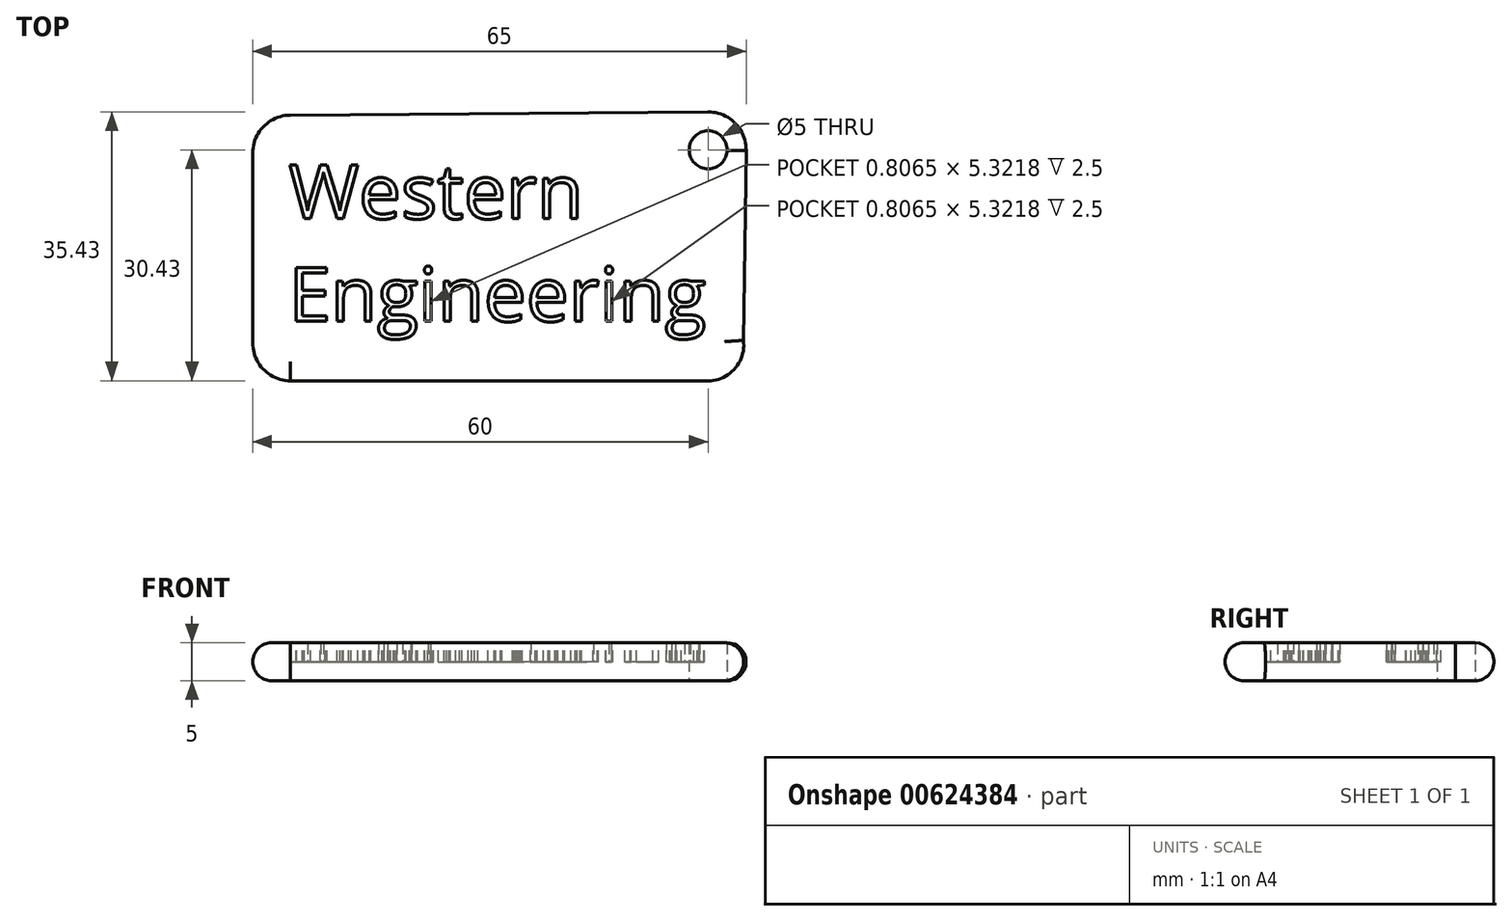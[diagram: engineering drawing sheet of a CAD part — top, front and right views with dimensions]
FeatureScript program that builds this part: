
annotation { "Feature Type Name" : "Feature", "Feature Type Description" : "" }
export const myFeature = defineFeature(function(context is Context, id is Id, definition is map)
    precondition{}
    {
        {
            var Q0;
            Q0=qCreatedBy(makeId("Top.planeOp"),FACE);
            var sketch = newSketch(context, id + "F0", { "sketchPlane" : qUnion([Q0])});
            skLineSegment(sketch, "E0", {"start": v(0, 5) * mm, "end": v(0, 30) * mm});
            skArc(sketch, "E1", {"start": v(0, 30) * mm, "mid": v(1.45, 33.52) * mm, "end": v(4.96, 35) * mm});
            skArc(sketch, "E2", {"start": v(0, 5) * mm, "mid": v(1.45, 1.48) * mm, "end": v(4.96, 0) * mm});
            skLineSegment(sketch, "E3", {"start": v(4.96, 35) * mm, "end": v(59.96, 35.43) * mm});
            skLineSegment(sketch, "E4", {"start": v(4.96, 0) * mm, "end": v(59.96, 0) * mm});
            skArc(sketch, "E5", {"start": v(59.96, 35.43) * mm, "mid": v(63.56, 33.94) * mm, "end": v(65, 30.33) * mm});
            skArc(sketch, "E6", {"start": v(59.96, 0) * mm, "mid": v(63.5, 1.6) * mm, "end": v(64.64, 5.33) * mm});
            skLineSegment(sketch, "E7", {"start": v(65, 30.33) * mm, "end": v(64.64, 5.33) * mm});
            skCircle(sketch, "E8", {"center": v(60, 30.43) * mm, "radius": 2.5 * mm});
            skSolve(sketch);
        }
        {
            var Q0;
            Q0=makeQuery(id+"F0.imprint","IMPRINT",FACE,{"disambiguationData":[TD([[makeQuery(id+"F0.imprint","IMPRINT",EDGE,{"derivedFrom":sQuery(id+"F0.wireOp",EDGE,"E0")}),-1.0]])]});
            extrude(context, id + "F1", {"entities" : qUnion([Q0]), "depth" : 5 * mm, "offsetDistance" : 25 * mm});
        }
        {
            var Q0;
            Q0=makeQuery(id+"F1.opExtrude","CAP_EDGE",EDGE,{"disambiguationData":[OSD([sQuery(id+"F0.wireOp",EDGE,"E3")])],"isStart":false});
            var Q1;
            Q1=makeQuery(id+"F1.opExtrude","CAP_EDGE",EDGE,{"disambiguationData":[OSD([sQuery(id+"F0.wireOp",EDGE,"E5")])],"isStart":false});
            var Q2;
            Q2=makeQuery(id+"F1.opExtrude","CAP_EDGE",EDGE,{"disambiguationData":[OSD([sQuery(id+"F0.wireOp",EDGE,"E7")])],"isStart":false});
            var Q3;
            Q3=makeQuery(id+"F1.opExtrude","CAP_EDGE",EDGE,{"disambiguationData":[OSD([sQuery(id+"F0.wireOp",EDGE,"E2")])],"isStart":false});
            var Q4;
            Q4=makeQuery(id+"F1.opExtrude","CAP_EDGE",EDGE,{"disambiguationData":[OSD([sQuery(id+"F0.wireOp",EDGE,"E1")])],"isStart":false});
            var Q5;
            Q5=makeQuery(id+"F1.opExtrude","CAP_EDGE",EDGE,{"disambiguationData":[OSD([sQuery(id+"F0.wireOp",EDGE,"E6")])],"isStart":false});
            fillet(context, id + "F2", {"entities" : qUnion([Q0, Q1, Q2, Q3, Q4, Q5]), "radius" : 2.5 * mm, "tangentPropagation" : true, "allowEdgeOverflow" : false});
        }
        {
            var Q0;
            Q0=makeQuery(id+"F1.opExtrude","CAP_EDGE",EDGE,{"disambiguationData":[OSD([sQuery(id+"F0.wireOp",EDGE,"E6")])],"isStart":true});
            var Q1;
            Q1=makeQuery(id+"F1.opExtrude","CAP_EDGE",EDGE,{"disambiguationData":[OSD([sQuery(id+"F0.wireOp",EDGE,"E7")])],"isStart":true});
            var Q2;
            Q2=makeQuery(id+"F1.opExtrude","CAP_EDGE",EDGE,{"disambiguationData":[OSD([sQuery(id+"F0.wireOp",EDGE,"E3")])],"isStart":true});
            var Q3;
            Q3=makeQuery(id+"F1.opExtrude","CAP_EDGE",EDGE,{"disambiguationData":[OSD([sQuery(id+"F0.wireOp",EDGE,"E5")])],"isStart":true});
            var Q4;
            Q4=makeQuery(id+"F1.opExtrude","CAP_EDGE",EDGE,{"disambiguationData":[OSD([sQuery(id+"F0.wireOp",EDGE,"E1")])],"isStart":true});
            var Q5;
            Q5=makeQuery(id+"F1.opExtrude","CAP_EDGE",EDGE,{"disambiguationData":[OSD([sQuery(id+"F0.wireOp",EDGE,"E0")])],"isStart":true});
            var Q6;
            Q6=makeQuery(id+"F1.opExtrude","CAP_EDGE",EDGE,{"disambiguationData":[OSD([sQuery(id+"F0.wireOp",EDGE,"E2")])],"isStart":true});
            fillet(context, id + "F3", {"entities" : qUnion([Q0, Q1, Q2, Q3, Q4, Q5, Q6]), "radius" : 2.5 * mm, "tangentPropagation" : true, "allowEdgeOverflow" : false});
        }
        {
            var Q0;
            Q0=makeQuery(id+"F1.opExtrude","CAP_FACE",FACE,{"disambiguationData":[OSD([sQuery(id+"F0.wireOp",EDGE,"E0"),sQuery(id+"F0.wireOp",EDGE,"E1"),sQuery(id+"F0.wireOp",EDGE,"E2"),sQuery(id+"F0.wireOp",EDGE,"E3"),sQuery(id+"F0.wireOp",EDGE,"E4"),sQuery(id+"F0.wireOp",EDGE,"E5"),sQuery(id+"F0.wireOp",EDGE,"E6"),sQuery(id+"F0.wireOp",EDGE,"E7")])],"isStart":false});
            var sketch = newSketch(context, id + "F4", { "sketchPlane" : qUnion([Q0])});
            skText(sketch, "E9", { "text": "Western\nEngineering", "fontName": "OpenSans-Regular.ttf"});
            const initialGuessF4  = {"E9": [0.00476, 0.02136, 1, 0, 0.00716]};
            skSetInitialGuess(sketch, initialGuessF4);
            skSolve(sketch);
        }
        {
            var Q0;
            Q0 = qSketchRegion(id + "F4", true);
            extrude(context, id + "F5", {"entities" : qUnion([Q0]), "operationType" : NewBodyOperationType.REMOVE, "oppositeDirection" : true, "depth" : 2.5 * mm, "offsetDistance" : 25 * mm});
        }
    });
